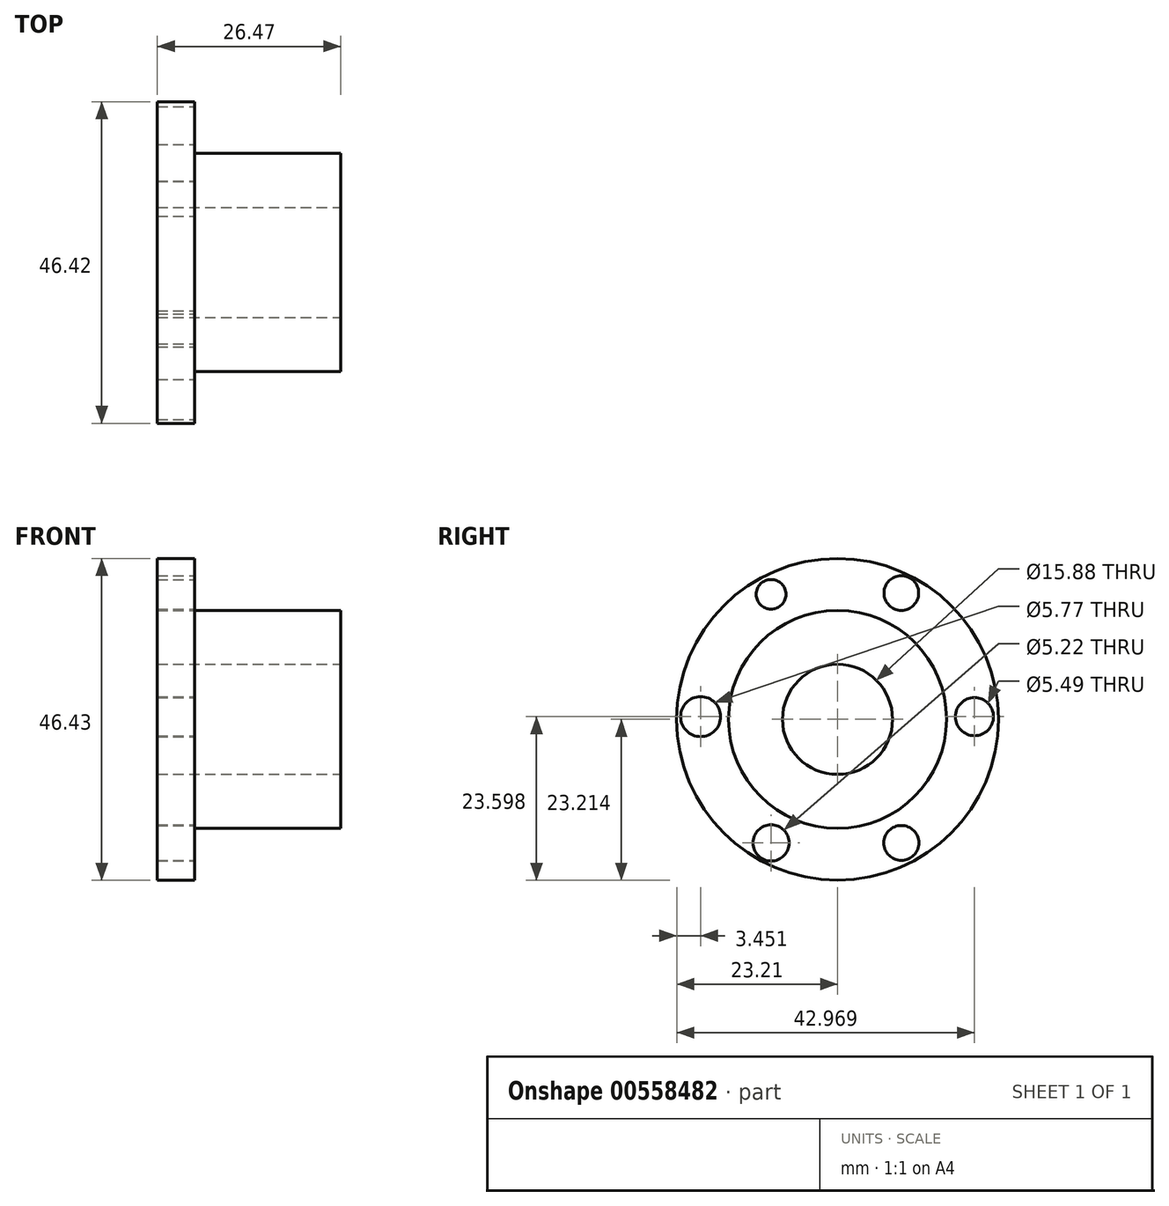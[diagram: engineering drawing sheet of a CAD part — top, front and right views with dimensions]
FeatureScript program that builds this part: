
annotation { "Feature Type Name" : "Feature", "Feature Type Description" : "" }
export const myFeature = defineFeature(function(context is Context, id is Id, definition is map)
    precondition{}
    {
        {
            var Q0;
            Q0=qCreatedBy(makeId("Front.planeOp"),FACE);
            var sketch = newSketch(context, id + "F0", { "sketchPlane" : qUnion([Q0])});
            skLineSegment(sketch, "E0", {"start": v(-48.34, 14.48) * mm, "end": v(-21.87, 14.48) * mm});
            skLineSegment(sketch, "E1", {"start": v(-21.87, 14.48) * mm, "end": v(-21.87, 22.54) * mm});
            skLineSegment(sketch, "E2", {"start": v(-21.87, 22.54) * mm, "end": v(-48.34, 22.54) * mm});
            skLineSegment(sketch, "E3", {"start": v(-48.34, 22.54) * mm, "end": v(-48.34, 14.48) * mm});
            skLineSegment(sketch, "E4", {"start": v(-21.87, 22.54) * mm, "end": v(-21.87, 30.21) * mm});
            skLineSegment(sketch, "E5", {"start": v(-21.87, 30.21) * mm, "end": v(-42.97, 30.21) * mm});
            skLineSegment(sketch, "E6", {"start": v(-42.97, 30.21) * mm, "end": v(-42.97, 37.7) * mm});
            skLineSegment(sketch, "E7", {"start": v(-42.97, 37.7) * mm, "end": v(-48.34, 37.7) * mm});
            skLineSegment(sketch, "E8", {"start": v(-48.34, 37.7) * mm, "end": v(-48.34, 22.54) * mm});
            skSolve(sketch);
        }
        {
            var Q0;
            Q0=makeQuery(id+"F0.imprint","IMPRINT",FACE,{"disambiguationData":[TD([[makeQuery(id+"F0.imprint","IMPRINT",EDGE,{"derivedFrom":sQuery(id+"F0.wireOp",EDGE,"E2")}),-1.0]])]});
            var Q1;
            Q1=makeQuery(id+"F0.imprint","IMPRINT",FACE,{"disambiguationData":[TD([[makeQuery(id+"F0.imprint","IMPRINT",EDGE,{"derivedFrom":sQuery(id+"F0.wireOp",EDGE,"E0")}),1.0]])]});
            var Q2;
            Q2=sQuery(id+"F0.wireOp",EDGE,"E0");
            revolve(context, id + "F1", {"entities" : qUnion([Q0, Q1]), "axis" : qUnion([Q2]), "revolveType" : RevolveType.FULL});
        }
        {
            var Q0;
            Q0=makeQuery(id+"F1.opRevolve","SWEPT_FACE",FACE,{"disambiguationData":[OSD([sQuery(id+"F0.wireOp",EDGE,"E1"),sQuery(id+"F0.wireOp",EDGE,"E4")])]});
            var sketch = newSketch(context, id + "F2", { "sketchPlane" : qUnion([Q0])});
            skCircle(sketch, "E9", {"center": v(0, 14.48) * mm, "radius": 7.94 * mm});
            skSolve(sketch);
        }
        {
            var Q0;
            Q0 = qSketchRegion(id + "F2", true);
            extrude(context, id + "F3", {"entities" : qUnion([Q0]), "operationType" : NewBodyOperationType.REMOVE, "endBound" : BoundingType.UP_TO_NEXT, "oppositeDirection" : true, "depth" : 25 * mm, "offsetDistance" : 25 * mm});
        }
        {
            var Q0;
            Q0=makeQuery(id+"F1.opRevolve","SWEPT_FACE",FACE,{"disambiguationData":[OSD([sQuery(id+"F0.wireOp",EDGE,"E6")])]});
            var sketch = newSketch(context, id + "F4", { "sketchPlane" : qUnion([Q0])});
            skCircle(sketch, "E10", {"center": v(0, 14.48) * mm, "radius": 20.16 * mm});
            skSolve(sketch);
        }
        {
            var Q0;
            Q0=makeQuery(id+"F4.imprint","IMPRINT",FACE,{"disambiguationData":[TD([[makeQuery(id+"F4.imprint","IMPRINT",EDGE,{"derivedFrom":sQuery(id+"F4.wireOp",EDGE,"E10")}),1.0]])]});
            var sketch = newSketch(context, id + "F5", { "sketchPlane" : qUnion([Q0])});
            skCircle(sketch, "E11", {"center": v(-9.6, 32.52) * mm, "radius": 2.14 * mm});
            skCircle(sketch, "E12", {"center": v(9.2, 32.7) * mm, "radius": 2.5 * mm});
            skCircle(sketch, "E13", {"center": v(-9.6, -3.36) * mm, "radius": 2.6 * mm});
            skCircle(sketch, "E14", {"center": v(9.2, -3.36) * mm, "radius": 2.52 * mm});
            skCircle(sketch, "E15", {"center": v(-19.76, 14.87) * mm, "radius": 2.88 * mm});
            skCircle(sketch, "E16", {"center": v(19.76, 14.87) * mm, "radius": 2.75 * mm});
            skSolve(sketch);
        }
        {
            var Q0;
            Q0 = qSketchRegion(id + "F5", true);
            extrude(context, id + "F6", {"entities" : qUnion([Q0]), "operationType" : NewBodyOperationType.REMOVE, "endBound" : BoundingType.UP_TO_NEXT, "oppositeDirection" : true, "depth" : 25 * mm, "offsetDistance" : 25 * mm});
        }
    });
